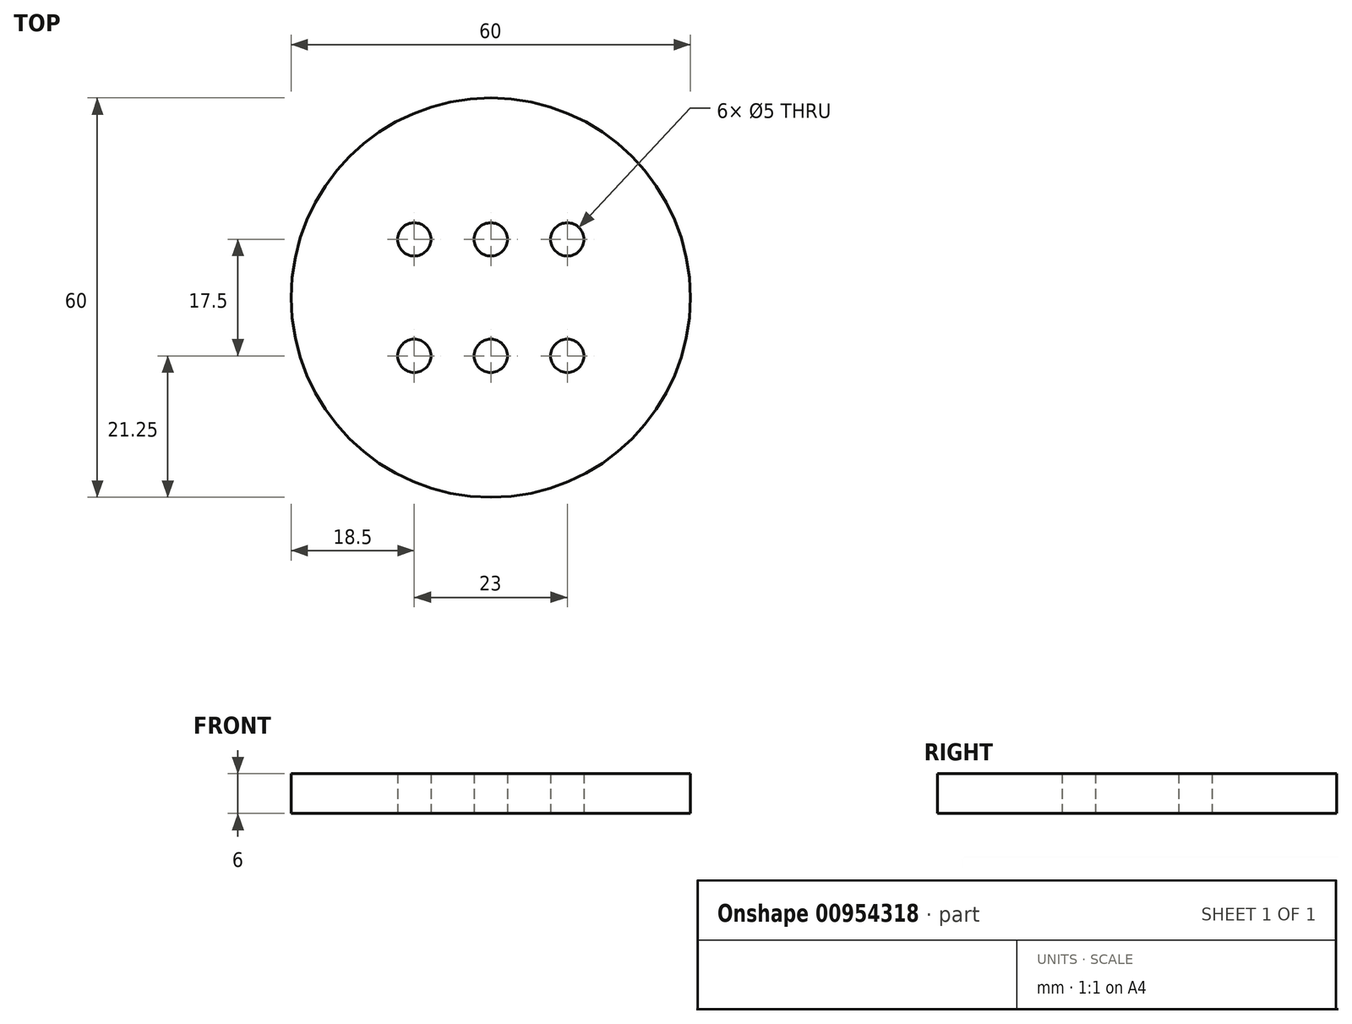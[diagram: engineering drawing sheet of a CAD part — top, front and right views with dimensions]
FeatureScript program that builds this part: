
annotation { "Feature Type Name" : "Feature", "Feature Type Description" : "" }
export const myFeature = defineFeature(function(context is Context, id is Id, definition is map)
    precondition{}
    {
        {
            var Q0;
            Q0=qCreatedBy(makeId("Top.planeOp"),FACE);
            var sketch = newSketch(context, id + "F0", { "sketchPlane" : qUnion([Q0])});
            skCircle(sketch, "E0", {"center": v(0, 0) * mm, "radius": 30 * mm});
            skCircle(sketch, "E1", {"center": v(-11.5, 8.75) * mm, "radius": 2.5 * mm});
            skCircle(sketch, "E2", {"center": v(11.5, 8.75) * mm, "radius": 2.5 * mm});
            skCircle(sketch, "E3", {"center": v(0, 8.75) * mm, "radius": 2.5 * mm});
            skCircle(sketch, "E4.MirrorC", {"center": v(-11.5, -8.75) * mm, "radius": 2.5 * mm});
            skCircle(sketch, "E5.MirrorC", {"center": v(0, -8.75) * mm, "radius": 2.5 * mm});
            skCircle(sketch, "E6.MirrorC", {"center": v(11.5, -8.75) * mm, "radius": 2.5 * mm});
            skSolve(sketch);
        }
        {
            var Q0;
            Q0=makeQuery(id+"F0.imprint","IMPRINT",FACE,{"disambiguationData":[TD([[makeQuery(id+"F0.imprint","IMPRINT",EDGE,{"derivedFrom":sQuery(id+"F0.wireOp",EDGE,"E0")}),1.0]])]});
            extrude(context, id + "F1", {"entities" : qUnion([Q0]), "depth" : 6 * mm, "offsetDistance" : 25 * mm});
        }
    });
